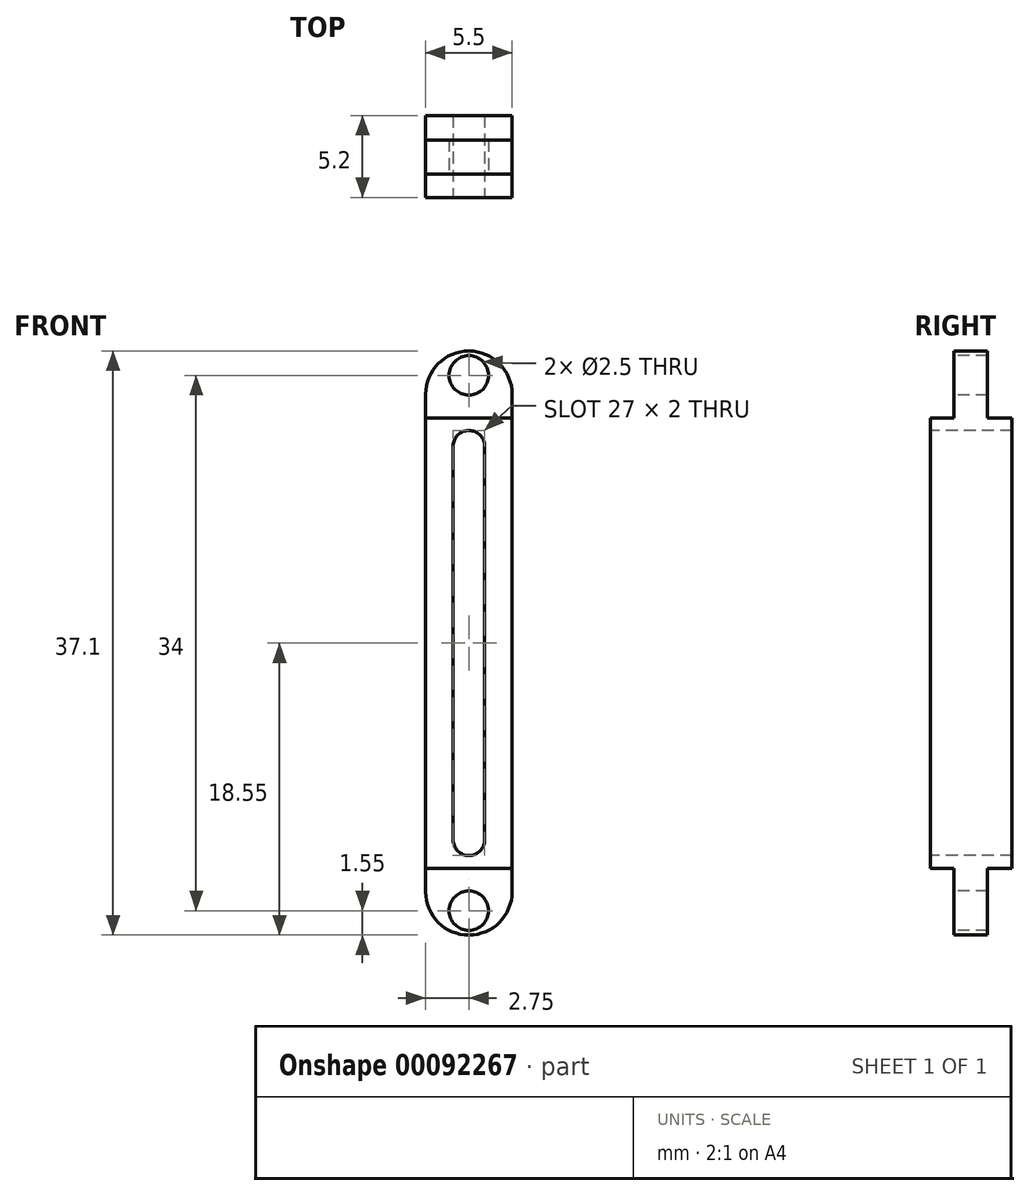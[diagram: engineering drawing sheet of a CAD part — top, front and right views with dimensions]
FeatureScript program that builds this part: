
annotation { "Feature Type Name" : "Feature", "Feature Type Description" : "" }
export const myFeature = defineFeature(function(context is Context, id is Id, definition is map)
    precondition{}
    {
        {
            var Q0;
            Q0=qCreatedBy(makeId("Front.planeOp"),FACE);
            var sketch = newSketch(context, id + "F0", { "sketchPlane" : qUnion([Q0])});
            skLineSegment(sketch, "E0.bottom", {"start": v(-2.75, 0) * mm, "end": v(2.75, 0) * mm});
            skLineSegment(sketch, "E0.top", {"start": v(-2.75, 14.3) * mm, "end": v(2.75, 14.3) * mm});
            skLineSegment(sketch, "E0.left", {"start": v(-2.75, 0) * mm, "end": v(-2.75, 14.3) * mm});
            skLineSegment(sketch, "E0.right", {"start": v(2.75, 0) * mm, "end": v(2.75, 14.3) * mm});
            skSolve(sketch);
        }
        {
            var Q0;
            Q0 = qSketchRegion(id + "F0", true);
            extrude(context, id + "F1", {"entities" : qUnion([Q0]), "depth" : 5.2 * mm});
        }
        {
            var Q0;
            Q0=makeQuery(id+"F1.opExtrude","CAP_FACE",FACE,{"disambiguationData":[OSD([sQuery(id+"F0.wireOp",EDGE,"E0.bottom"),sQuery(id+"F0.wireOp",EDGE,"E0.top"),sQuery(id+"F0.wireOp",EDGE,"E0.left"),sQuery(id+"F0.wireOp",EDGE,"E0.right")])],"isStart":false});
            var sketch = newSketch(context, id + "F2", { "sketchPlane" : qUnion([Q0])});
            skLineSegment(sketch, "E1.bottom", {"start": v(-1, 0) * mm, "end": v(1, 0) * mm});
            skLineSegment(sketch, "E1.top", {"start": v(-1, 12.5) * mm, "end": v(1, 12.5) * mm});
            skLineSegment(sketch, "E1.left", {"start": v(-1, 0) * mm, "end": v(-1, 12.5) * mm});
            skLineSegment(sketch, "E1.right", {"start": v(1, 0) * mm, "end": v(1, 12.5) * mm});
            skArc(sketch, "E2", {"start": v(1, 12.5) * mm, "mid": v(0, 13.5) * mm, "end": v(-1, 12.5) * mm});
            skSolve(sketch);
        }
        {
            var Q0;
            Q0 = qSketchRegion(id + "F2", true);
            extrude(context, id + "F3", {"entities" : qUnion([Q0]), "operationType" : NewBodyOperationType.REMOVE, "oppositeDirection" : true, "depth" : 5.5 * mm});
        }
        {
            var Q0;
            Q0=qCreatedBy(makeId("Front.planeOp"),FACE);
            cPlane(context, id + "F4", {"entities" : qUnion([Q0]), "cplaneType" : CPlaneType.OFFSET, "offset" : 1.55 * mm, "width" : 150 * mm, "height" : 150 * mm});
        }
        {
            var Q0;
            Q0=qCreatedBy(id+"F4.planeOp",FACE);
            var sketch = newSketch(context, id + "F5", { "sketchPlane" : qUnion([Q0])});
            skLineSegment(sketch, "E3.bottom", {"start": v(-2.75, 14.3) * mm, "end": v(2.75, 14.3) * mm});
            skLineSegment(sketch, "E3.top", {"start": v(-2.75, 15.8) * mm, "end": v(2.75, 15.8) * mm});
            skLineSegment(sketch, "E3.left", {"start": v(-2.75, 14.3) * mm, "end": v(-2.75, 15.8) * mm});
            skLineSegment(sketch, "E3.right", {"start": v(2.75, 14.3) * mm, "end": v(2.75, 15.8) * mm});
            skArc(sketch, "E4", {"start": v(2.75, 15.8) * mm, "mid": v(0, 18.55) * mm, "end": v(-2.75, 15.8) * mm});
            skSolve(sketch);
        }
        {
            var Q0;
            Q0 = qSketchRegion(id + "F5", true);
            extrude(context, id + "F6", {"entities" : qUnion([Q0]), "operationType" : NewBodyOperationType.ADD, "depth" : 2.15 * mm});
        }
        {
            var Q0;
            Q0=makeQuery(id+"F6.opExtrude","CAP_FACE",FACE,{"disambiguationData":[OSD([sQuery(id+"F5.wireOp",EDGE,"E3.bottom"),sQuery(id+"F5.wireOp",EDGE,"E3.left"),sQuery(id+"F5.wireOp",EDGE,"E3.right"),sQuery(id+"F5.wireOp",EDGE,"E4")])],"isStart":false});
            var sketch = newSketch(context, id + "F7", { "sketchPlane" : qUnion([Q0])});
            skCircle(sketch, "E5", {"center": v(0, 17) * mm, "radius": 1.25 * mm});
            skSolve(sketch);
        }
        {
            var Q0;
            Q0 = qSketchRegion(id + "F7", true);
            var Q1;
            Q1=sQuery(id+"F7.wireOp",EDGE,"E5");
            extrude(context, id + "F8", {"entities" : qUnion([Q0]), "operationType" : NewBodyOperationType.REMOVE, "surfaceEntities" : qUnion([Q1]), "oppositeDirection" : true, "depth" : 3 * mm});
        }
        {
            var Q0;
            Q0=makeQuery(id+"F1.opExtrude","SWEPT_BODY",BODY,{"disambiguationData":[OSD([sQuery(id+"F0.wireOp",EDGE,"E0.bottom"),sQuery(id+"F0.wireOp",EDGE,"E0.top"),sQuery(id+"F0.wireOp",EDGE,"E0.left"),sQuery(id+"F0.wireOp",EDGE,"E0.right")])]});
            var Q1;
            Q1=qCreatedBy(makeId("Top.planeOp"),FACE);
            mirror(context, id + "F9", {"operationType" : NewBodyOperationType.ADD, "entities" : qUnion([Q0]), "mirrorPlane" : qUnion([Q1])});
        }
    });
